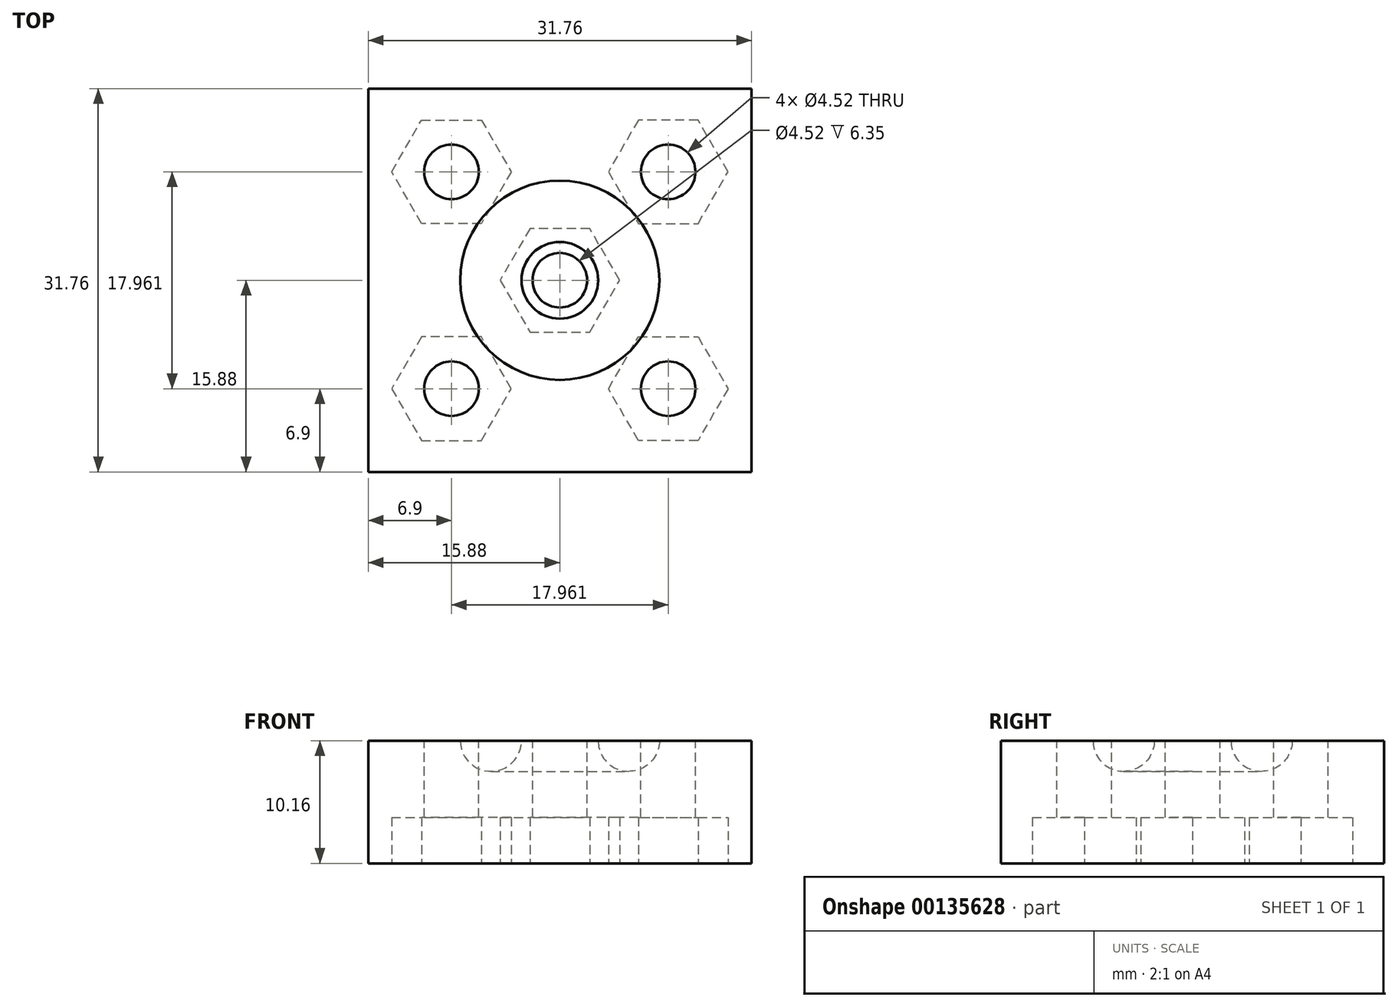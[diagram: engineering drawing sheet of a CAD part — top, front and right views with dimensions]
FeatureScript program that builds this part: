
annotation { "Feature Type Name" : "Feature", "Feature Type Description" : "" }
export const myFeature = defineFeature(function(context is Context, id is Id, definition is map)
    precondition{}
    {
        {
            var Q0;
            Q0=qCreatedBy(makeId("Top.planeOp"),FACE);
            var sketch = newSketch(context, id + "F0", { "sketchPlane" : qUnion([Q0])});
            skLineSegment(sketch, "E0.bottom", {"start": v(15.87, -15.87) * mm, "end": v(-15.88, -15.88) * mm});
            skLineSegment(sketch, "E0.top", {"start": v(15.87, 15.88) * mm, "end": v(-15.88, 15.88) * mm});
            skLineSegment(sketch, "E0.left", {"start": v(15.87, -15.88) * mm, "end": v(15.87, 15.88) * mm});
            skLineSegment(sketch, "E0.right", {"start": v(-15.88, -15.88) * mm, "end": v(-15.88, 15.88) * mm});
            skPoint(sketch, "E0.middle", {"position": v(0, 0) * mm});
            skSolve(sketch);
        }
        {
            var Q0;
            Q0=makeQuery(id+"F0.imprint","IMPRINT",FACE,{"disambiguationData":[TD([[makeQuery(id+"F0.imprint","IMPRINT",EDGE,{"derivedFrom":sQuery(id+"F0.wireOp",EDGE,"E0.bottom")}),-1.0]])]});
            extrude(context, id + "F1", {"entities" : qUnion([Q0]), "depth" : 10.16 * mm});
        }
        {
            var Q0;
            Q0=qCreatedBy(makeId("Front.planeOp"),FACE);
            var sketch = newSketch(context, id + "F2", { "sketchPlane" : qUnion([Q0])});
            skCircle(sketch, "E1", {"center": v(5.72, 10.16) * mm, "radius": 2.54 * mm});
            skLineSegment(sketch, "E2", {"start": v(0, 16.12) * mm, "end": v(0, 0) * mm, "construction": true});
            skSolve(sketch);
        }
        {
            var Q0;
            Q0=makeQuery(id+"F2.imprint","IMPRINT",FACE,{"disambiguationData":[TD([[makeQuery(id+"F2.imprint","IMPRINT",EDGE,{"derivedFrom":sQuery(id+"F2.wireOp",EDGE,"E1")}),1.0]])]});
            var Q1;
            Q1=sQuery(id+"F2.wireOp",EDGE,"E2");
            revolve(context, id + "F3", {"operationType" : NewBodyOperationType.REMOVE, "entities" : qUnion([Q0]), "axis" : qUnion([Q1]), "revolveType" : RevolveType.FULL, "oppositeDirection" : true});
        }
        {
            var Q0;
            {var subQ0=sQuery(id+"F0.wireOp",EDGE,"E0.right");var subQ1=sQuery(id+"F0.wireOp",EDGE,"E0.left");var subQ2=sQuery(id+"F0.wireOp",EDGE,"E0.top");var subQ3=sQuery(id+"F0.wireOp",EDGE,"E0.bottom");Q0=makeQuery(id+"F3.boolean.opBoolean","SPLIT",FACE,{"disambiguationData":[TD([makeQuery(id+"F1.opExtrude","SWEPT_FACE",FACE,{"disambiguationData":[OSD([subQ3])]}),makeQuery(id+"F1.opExtrude","SWEPT_FACE",FACE,{"disambiguationData":[OSD([subQ2])]}),makeQuery(id+"F1.opExtrude","SWEPT_FACE",FACE,{"disambiguationData":[OSD([subQ1])]}),makeQuery(id+"F1.opExtrude","SWEPT_FACE",FACE,{"disambiguationData":[OSD([subQ0])]}),makeQuery(id+"F3.opRevolve","SWEPT_FACE",FACE,{"disambiguationData":[OSD([sQuery(id+"F2.wireOp",EDGE,"E1")])]})])],"derivedFrom":makeQuery(id+"F1.opExtrude","CAP_FACE",FACE,{"disambiguationData":[OSD([subQ3,subQ2,subQ1,subQ0])],"isStart":false})});}
            var sketch = newSketch(context, id + "F4", { "sketchPlane" : qUnion([Q0])});
            skLineSegment(sketch, "E3", {"start": v(-15.88, 15.88) * mm, "end": v(15.88, -15.88) * mm, "construction": true});
            skLineSegment(sketch, "E4", {"start": v(15.88, 15.88) * mm, "end": v(-15.88, -15.88) * mm, "construction": true});
            skCircle(sketch, "E5", {"center": v(0, 0) * mm, "radius": 2.26 * mm});
            skCircle(sketch, "E6", {"center": v(-8.98, 8.98) * mm, "radius": 2.26 * mm});
            skLineSegment(sketch, "E7", {"start": v(0, 15.88) * mm, "end": v(0, -15.88) * mm, "construction": true});
            skLineSegment(sketch, "E8", {"start": v(-15.88, 0) * mm, "end": v(15.88, 0) * mm, "construction": true});
            skCircle(sketch, "E9.MirrorC", {"center": v(8.98, 8.98) * mm, "radius": 2.26 * mm});
            skCircle(sketch, "E10.MirrorC", {"center": v(-8.98, -8.98) * mm, "radius": 2.26 * mm});
            skCircle(sketch, "E11.MirrorC", {"center": v(8.98, -8.98) * mm, "radius": 2.26 * mm});
            skSolve(sketch);
        }
        {
            var Q0;
            Q0 = qSketchRegion(id + "F4", true);
            extrude(context, id + "F5", {"entities" : qUnion([Q0]), "operationType" : NewBodyOperationType.REMOVE, "oppositeDirection" : true, "depth" : 25.4 * mm});
        }
        {
            var Q0;
            Q0=makeQuery(id+"F1.opExtrude","CAP_FACE",FACE,{"disambiguationData":[OSD([sQuery(id+"F0.wireOp",EDGE,"E0.bottom"),sQuery(id+"F0.wireOp",EDGE,"E0.top"),sQuery(id+"F0.wireOp",EDGE,"E0.left"),sQuery(id+"F0.wireOp",EDGE,"E0.right")])],"isStart":true});
            var sketch = newSketch(context, id + "F6", { "sketchPlane" : qUnion([Q0])});
            skCircle(sketch, "E12.cCircle", {"center": v(0, 0) * mm, "radius": 4.95 * mm, "construction": true});
            skLineSegment(sketch, "E12.0", {"start": v(2.48, -4.29) * mm, "end": v(-2.48, -4.29) * mm});
            skLineSegment(sketch, "E12.1", {"start": v(-2.48, -4.29) * mm, "end": v(-4.95, 0) * mm});
            skLineSegment(sketch, "E12.2", {"start": v(-4.95, 0) * mm, "end": v(-2.48, 4.29) * mm});
            skLineSegment(sketch, "E12.3", {"start": v(-2.48, 4.29) * mm, "end": v(2.48, 4.29) * mm});
            skLineSegment(sketch, "E12.4", {"start": v(2.48, 4.29) * mm, "end": v(4.95, 0) * mm});
            skLineSegment(sketch, "E12.5", {"start": v(4.95, 0) * mm, "end": v(2.48, -4.29) * mm});
            skCircle(sketch, "E13.cCircle", {"center": v(-8.98, 8.98) * mm, "radius": 4.95 * mm, "construction": true});
            skLineSegment(sketch, "E13.0", {"start": v(-6.5, 4.7) * mm, "end": v(-11.46, 4.7) * mm});
            skLineSegment(sketch, "E13.1", {"start": v(-11.46, 4.7) * mm, "end": v(-13.93, 8.98) * mm});
            skLineSegment(sketch, "E13.2", {"start": v(-13.93, 8.98) * mm, "end": v(-11.46, 13.27) * mm});
            skLineSegment(sketch, "E13.3", {"start": v(-11.46, 13.27) * mm, "end": v(-6.5, 13.27) * mm});
            skLineSegment(sketch, "E13.4", {"start": v(-6.5, 13.27) * mm, "end": v(-4.03, 8.98) * mm});
            skLineSegment(sketch, "E13.5", {"start": v(-4.03, 8.98) * mm, "end": v(-6.5, 4.7) * mm});
            skLineSegment(sketch, "E14.MirrorCS", {"start": v(6.5, 13.27) * mm, "end": v(4.03, 8.98) * mm});
            skLineSegment(sketch, "E15.MirrorCS", {"start": v(6.5, 4.7) * mm, "end": v(11.46, 4.7) * mm});
            skLineSegment(sketch, "E16.MirrorCS", {"start": v(4.03, 8.98) * mm, "end": v(6.5, 4.7) * mm});
            skLineSegment(sketch, "E17.MirrorCS", {"start": v(11.46, 13.27) * mm, "end": v(6.5, 13.27) * mm});
            skLineSegment(sketch, "E18.MirrorCS", {"start": v(13.93, 8.98) * mm, "end": v(11.46, 13.27) * mm});
            skLineSegment(sketch, "E19.MirrorCS", {"start": v(11.46, 4.7) * mm, "end": v(13.93, 8.98) * mm});
            skLineSegment(sketch, "E20.MirrorCS", {"start": v(6.5, -13.27) * mm, "end": v(4.03, -8.98) * mm});
            skCircle(sketch, "E21.MirrorC", {"center": v(-8.98, -8.98) * mm, "radius": 4.95 * mm, "construction": true});
            skLineSegment(sketch, "E22.MirrorCS", {"start": v(-6.5, -4.7) * mm, "end": v(-11.46, -4.7) * mm});
            skLineSegment(sketch, "E23.MirrorCS", {"start": v(-11.46, -4.7) * mm, "end": v(-13.93, -8.98) * mm});
            skLineSegment(sketch, "E24.MirrorCS", {"start": v(4.03, -8.98) * mm, "end": v(6.5, -4.7) * mm});
            skLineSegment(sketch, "E25.MirrorCS", {"start": v(-13.93, -8.98) * mm, "end": v(-11.46, -13.27) * mm});
            skLineSegment(sketch, "E26.MirrorCS", {"start": v(-11.46, -13.27) * mm, "end": v(-6.5, -13.27) * mm});
            skLineSegment(sketch, "E27.MirrorCS", {"start": v(-6.5, -13.27) * mm, "end": v(-4.03, -8.98) * mm});
            skLineSegment(sketch, "E28.MirrorCS", {"start": v(11.46, -13.27) * mm, "end": v(6.5, -13.27) * mm});
            skLineSegment(sketch, "E29.MirrorCS", {"start": v(11.46, -4.7) * mm, "end": v(13.93, -8.98) * mm});
            skLineSegment(sketch, "E30.MirrorCS", {"start": v(13.93, -8.98) * mm, "end": v(11.46, -13.27) * mm});
            skLineSegment(sketch, "E31.MirrorCS", {"start": v(-4.03, -8.98) * mm, "end": v(-6.5, -4.7) * mm});
            skLineSegment(sketch, "E32.MirrorCS", {"start": v(6.5, -4.7) * mm, "end": v(11.46, -4.7) * mm});
            skSolve(sketch);
        }
        {
            var Q0;
            Q0 = qSketchRegion(id + "F6", true);
            extrude(context, id + "F7", {"entities" : qUnion([Q0]), "operationType" : NewBodyOperationType.REMOVE, "oppositeDirection" : true, "depth" : 3.8 * mm});
        }
    });
